# Revit family: Faucet-Two_Handle-American_Standard-Glenmere-7617807_Series
name_source: partatom
category: Plumbing Fixtures
revit_build: Autodesk Revit 2018 (Build: 20170223_1515(x64)
units: mm (PartAtom-declared; Revit-internal decimal feet)

## family parameters
Always vertical = No
Cut with Voids When Loaded = Yes
OmniClass Number = 23.45.55.17
OmniClass Title = Mixing Faucets
Part Type = Normal
Room Calculation Point = No
Round Connector Dimension = Use Diameter
Shared = Yes
Work Plane-Based = Yes

## types (4) — shared parameters
ADA Compliant = Yes
Assembly Code = D2020300
CEC Compliant = Yes
CWFU = 1.5
Cold Water Connection Diameter = 3/8"
Default Elevation = 0"
Description = Glenmere Single-Handle Bathroom Faucet
Flow Rate = 1.2 gpm (4.5L/min)
HWFU = 1.5
Height = 6 5/16"
Hot Water Connection Diameter = 3/8"
Installation Type = Deck Mounted
Length = 6 1/8"
M953456-2950A Pop Up Drain = Yes
Manufacturer = American Standard
Pop Up Drain Depth = 3"
Pop Up Drain Width = 5"
Product Documentation Link = https://americanstandard.box.com
Product Page URL = https://www.americanstandard-us.com
URL = http://www.americanstandard-us.com
Vent Connection = No
Warranty Information = Limited Lifetime Warranty
Waste Connection = No
Width = 13 1/4"
zero-valued in all types: WFU

## per-type parameters (varying)
| type | CW Connection | Finish | HW Connection | Material |
| 7617807.002 | Yes | Metal-American Standard-002-Polished Chrome | Yes | Metal-American Standard-002-Polished Chrome |
| 7617807.295 | No | Metal-American Standard-295-Brushed Nickel | No | Metal-American Standard-295-Brushed Nickel |
| 7617807.243 | No | Metal-American Standard-243-Matte Black | No | Metal-American Standard-243-Matte Black |
| 7617807.278 | No | Metal-American Standard-278-Legacy Bronze | No | Metal-American Standard-278-Legacy Bronze |

note: column(s) folded — value = type name in every type: Model

## geometry (parser evidence)
native form markers: Sweep x3
no freeform markers — native parametric forms only
